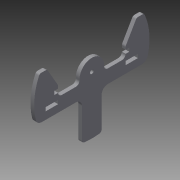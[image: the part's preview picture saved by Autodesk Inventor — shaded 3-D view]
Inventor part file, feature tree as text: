
AUTODESK INVENTOR PART (.ipt)
format: ipt  version: 2013 SP1 (Build 170176100, 176)  size: 172,544 bytes
history: native  units: mm
features: extrude x1
ambient origin geometry x8: Origin, YZ Plane, XZ Plane, XY Plane, X Axis, Y Axis, Z Axis, Center Point
feature tree (1):
  extrude  "Extrusion5"  Depth=94.0mm
